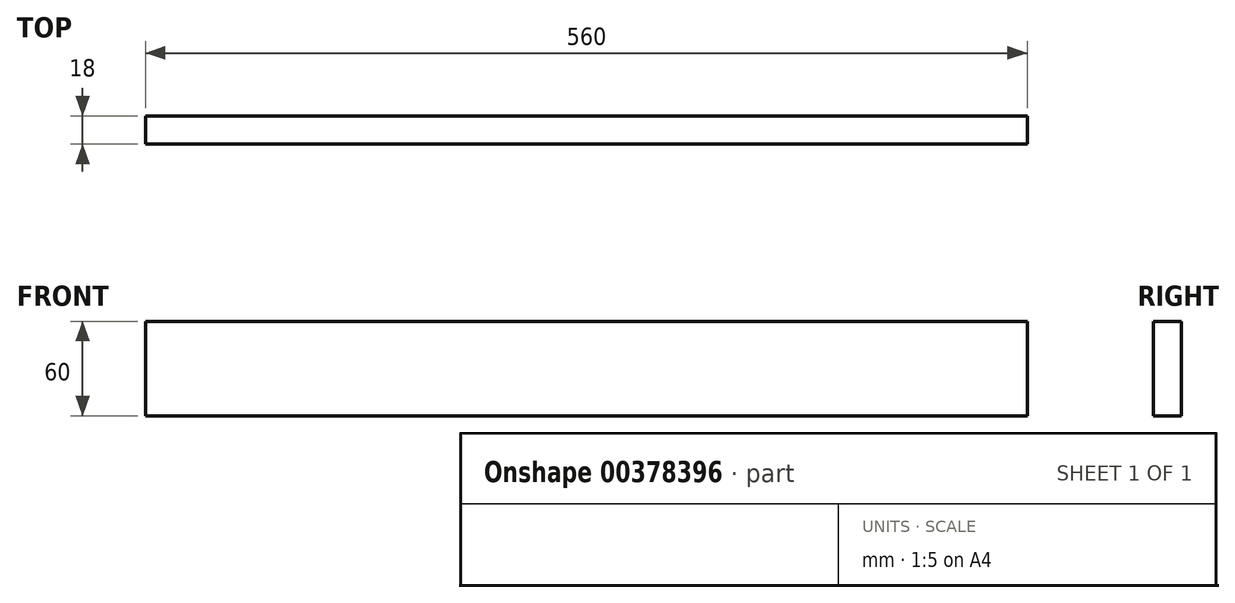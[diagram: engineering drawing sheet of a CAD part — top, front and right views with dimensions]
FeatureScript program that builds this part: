
annotation { "Feature Type Name" : "Feature", "Feature Type Description" : "" }
export const myFeature = defineFeature(function(context is Context, id is Id, definition is map)
    precondition{}
    {
        {
            var Q0;
            Q0=qCreatedBy(makeId("Right.planeOp"),FACE);
            var sketch = newSketch(context, id + "F0", { "sketchPlane" : qUnion([Q0])});
            skLineSegment(sketch, "E0.bottom", {"start": v(9, 30) * mm, "end": v(-9, 30) * mm});
            skLineSegment(sketch, "E0.top", {"start": v(9, -30) * mm, "end": v(-9, -30) * mm});
            skLineSegment(sketch, "E0.left", {"start": v(9, 30) * mm, "end": v(9, -30) * mm});
            skLineSegment(sketch, "E0.right", {"start": v(-9, 30) * mm, "end": v(-9, -30) * mm});
            skPoint(sketch, "E0.middle", {"position": v(0, 0) * mm});
            skSolve(sketch);
        }
        {
            var Q0;
            Q0=qSketchRegion(id+"F0",true);
            extrude(context, id + "F1", {"entities" : qUnion([Q0]), "depth" : 560 * mm});
        }
    });
